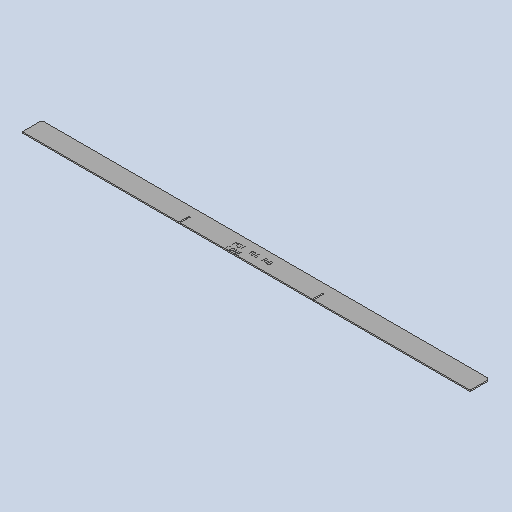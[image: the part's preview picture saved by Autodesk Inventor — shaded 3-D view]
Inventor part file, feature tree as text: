
AUTODESK INVENTOR PART (.ipt)
format: ipt  version: 2025 (Build 290162010, 162A)  size: 421,376 bytes
history: native  units: mm
features: other x5, sketch x4, extrude x2, sheet_metal_op x1, projected_geometry x1
ambient origin geometry x8: Origin, YZ Plane, XZ Plane, XY Plane, X Axis, Y Axis, Z Axis, Center Point
bodies: Body1 (feature_tree)
feature tree (13):
  sheet_metal_op  "Face1"
  extrude  "Extrusion2"  Depth=1200.0mm
  extrude  "Extrusion3"  Depth=50.0mm
  other  "Mark1"
  other  "Corner Chamfer1"
  other  "A-Side Definition"
  sketch  "Sketch1"  dims[d18=50.0mm d19=1200.0mm]
  other  "Plate2"
  sketch  "Sketch3"  dims[d20=3.0mm d25=50.0mm]
  sketch  "Sketch4"  dims[d26=50.0mm]
  projected_geometry  "Projected Loop1"
  sketch  "Sketch5"  dims[d28=3.1mm d29=26.0mm d30=0.0mm d31=0.0mm d39=12.217305mm d40=35.0mm d45=25.0mm d46=25.0mm d47=0.0mm d48=0.0mm d49=6.0mm d50=6.0mm d51=45.0deg d52=340.0mm]
  other  "Definition1"
